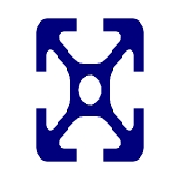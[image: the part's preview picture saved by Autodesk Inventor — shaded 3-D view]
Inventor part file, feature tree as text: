
AUTODESK INVENTOR PART (.ipt)
format: ipt  version: 2020 (Build 240168000, 168)  size: 274,432 bytes
history: native  units: mm
features: other x16, sketch x8
ambient origin geometry x8: Origin, YZ Plane, XZ Plane, XY Plane, X Axis, Y Axis, Z Axis, Center Point
bodies: Body (feature_tree)
feature tree (24):
  other  "Řízená délka"
  other  "Těleso1"
  other  "Start Plane"
  other  "End Plane"
  other  "iFeatureSketch"
  other  "DRAZKA_20:1"
  other  "DRAZKA_20:2"
  other  "DRAZKA_20:3"
  other  "DRAZKA_20:4"
  other  "DIRA_20:1"
  other  "DRAZKA_20:1Axis"
  other  "DRAZKA_20:2Axis"
  other  "DRAZKA_20:3Axis"
  other  "DRAZKA_20:4Axis"
  other  "DIRA_20:1Axis"
  sketch  "Sketch"  dims[d2=20.0mm d3=20.0mm d4=2.0mm d9=-0.0mm d10=450.0mm d11=0.13mm d12=0.0mm d15=0.83mm d16=0.83mm d17=9.8mm d18=3.0mm d19=4.55mm d20=45.0deg d21=5.2mm d22=1.8mm d24=1.0mm d26=0.83mm d27=0.83mm d28=9.8mm d29=3.0mm d30=4.55mm d31=45.0deg d32=5.2mm d33=1.8mm d35=1.0mm d37=0.83mm d38=0.83mm d39=9.8mm d40=3.0mm d41=4.55mm d42=45.0deg d43=5.2mm d44=1.8mm d46=1.0mm d48=0.83mm d49=0.83mm d50=9.8mm d51=3.0mm d52=4.55mm d53=45.0deg d54=5.2mm d55=1.8mm d57=1.0mm d59=4.3mm d60=0.0mm d61=0.0mm d62=0.0mm d63=0.0mm d64=0.0mm d65=0.0mm d66=0.0mm d67=0.0mm d76=90.0deg d14=450.0mm]
  sketch  "Náčrt11"
  other  "Pracovní rovina4"
  sketch  "Náčrt12"
  sketch  "Náčrt6"
  sketch  "Náčrt7"
  sketch  "Náčrt8"
  sketch  "Náčrt9"
  sketch  "Náčrt10"
